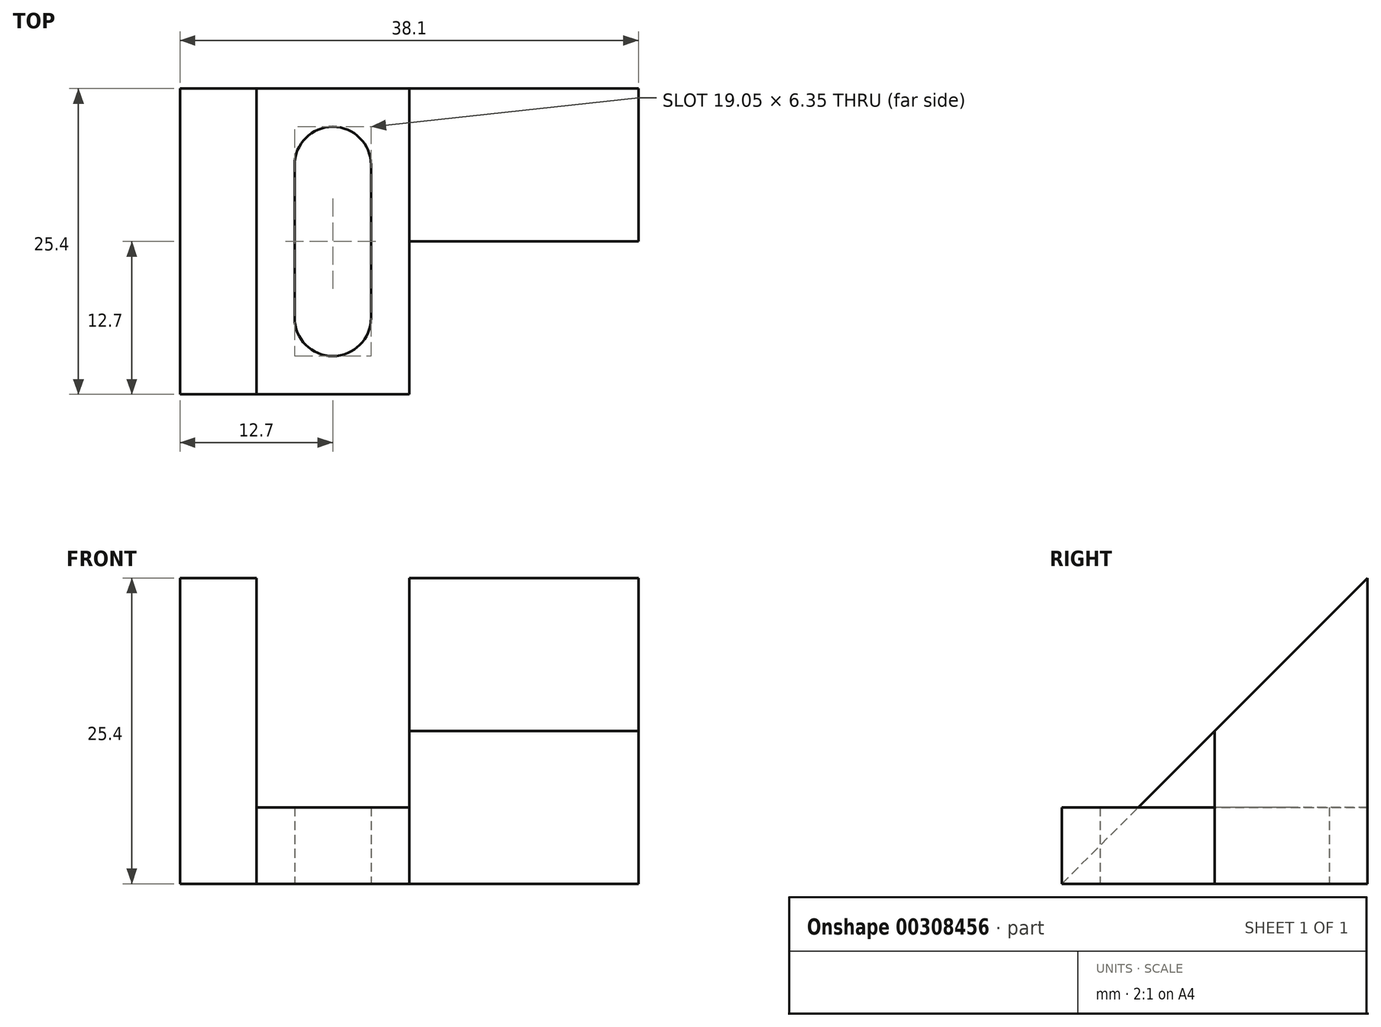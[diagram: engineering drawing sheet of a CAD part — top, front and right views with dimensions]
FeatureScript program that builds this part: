
annotation { "Feature Type Name" : "Feature", "Feature Type Description" : "" }
export const myFeature = defineFeature(function(context is Context, id is Id, definition is map)
    precondition{}
    {
        {
            var Q0;
            Q0=qCreatedBy(makeId("Right.planeOp"),FACE);
            var sketch = newSketch(context, id + "F0", { "sketchPlane" : qUnion([Q0])});
            skLineSegment(sketch, "E0", {"start": v(0, 0) * mm, "end": v(25.4, 25.4) * mm});
            skLineSegment(sketch, "E1", {"start": v(25.4, 25.4) * mm, "end": v(25.4, 0) * mm});
            skLineSegment(sketch, "E2", {"start": v(25.4, 0) * mm, "end": v(0, 0) * mm});
            skSolve(sketch);
        }
        {
            var Q0;
            Q0 = qSketchRegion(id + "F0", true);
            extrude(context, id + "F1", {"entities" : qUnion([Q0]), "depth" : 6.35 * mm});
        }
        {
            var Q0;
            Q0=qCreatedBy(makeId("Top.planeOp"),FACE);
            var sketch = newSketch(context, id + "F2", { "sketchPlane" : qUnion([Q0])});
            skLineSegment(sketch, "E3", {"start": v(6.35, 25.4) * mm, "end": v(19.05, 25.4) * mm});
            skLineSegment(sketch, "E4", {"start": v(19.05, 25.4) * mm, "end": v(19.05, 0) * mm});
            skLineSegment(sketch, "E5", {"start": v(19.05, 0) * mm, "end": v(6.35, 0) * mm});
            skLineSegment(sketch, "E6", {"start": v(6.35, 0) * mm, "end": v(6.35, 25.4) * mm});
            skLineSegment(sketch, "E7", {"start": v(9.52, 19.05) * mm, "end": v(9.53, 6.35) * mm});
            skArc(sketch, "E8", {"start": v(9.53, 6.35) * mm, "mid": v(12.7, 3.18) * mm, "end": v(15.88, 6.35) * mm});
            skLineSegment(sketch, "E9", {"start": v(15.88, 6.35) * mm, "end": v(15.88, 19.05) * mm});
            skArc(sketch, "E10", {"start": v(15.88, 19.05) * mm, "mid": v(12.7, 22.22) * mm, "end": v(9.52, 19.05) * mm});
            skLineSegment(sketch, "E11", {"start": v(12.7, 25.4) * mm, "end": v(12.7, 0) * mm, "construction": true});
            skSolve(sketch);
        }
        {
            var Q0;
            Q0 = qSketchRegion(id + "F2", true);
            extrude(context, id + "F3", {"entities" : qUnion([Q0]), "operationType" : NewBodyOperationType.ADD, "depth" : 6.35 * mm});
        }
        {
            var Q0;
            Q0=makeQuery(id+"F3.opExtrude","SWEPT_FACE",FACE,{"disambiguationData":[OSD([sQuery(id+"F2.wireOp",EDGE,"E4")])]});
            var sketch = newSketch(context, id + "F4", { "sketchPlane" : qUnion([Q0])});
            skLineSegment(sketch, "E12", {"start": v(25.4, 25.4) * mm, "end": v(25.4, 0) * mm});
            skLineSegment(sketch, "E13", {"start": v(25.4, 0) * mm, "end": v(12.7, 0) * mm});
            skLineSegment(sketch, "E14", {"start": v(12.7, 0) * mm, "end": v(12.7, 12.7) * mm});
            skLineSegment(sketch, "E15", {"start": v(12.7, 12.7) * mm, "end": v(25.4, 25.4) * mm});
            skSolve(sketch);
        }
        {
            var Q0;
            Q0 = qSketchRegion(id + "F4", true);
            extrude(context, id + "F5", {"entities" : qUnion([Q0]), "operationType" : NewBodyOperationType.ADD, "depth" : 19.05 * mm});
        }
    });
